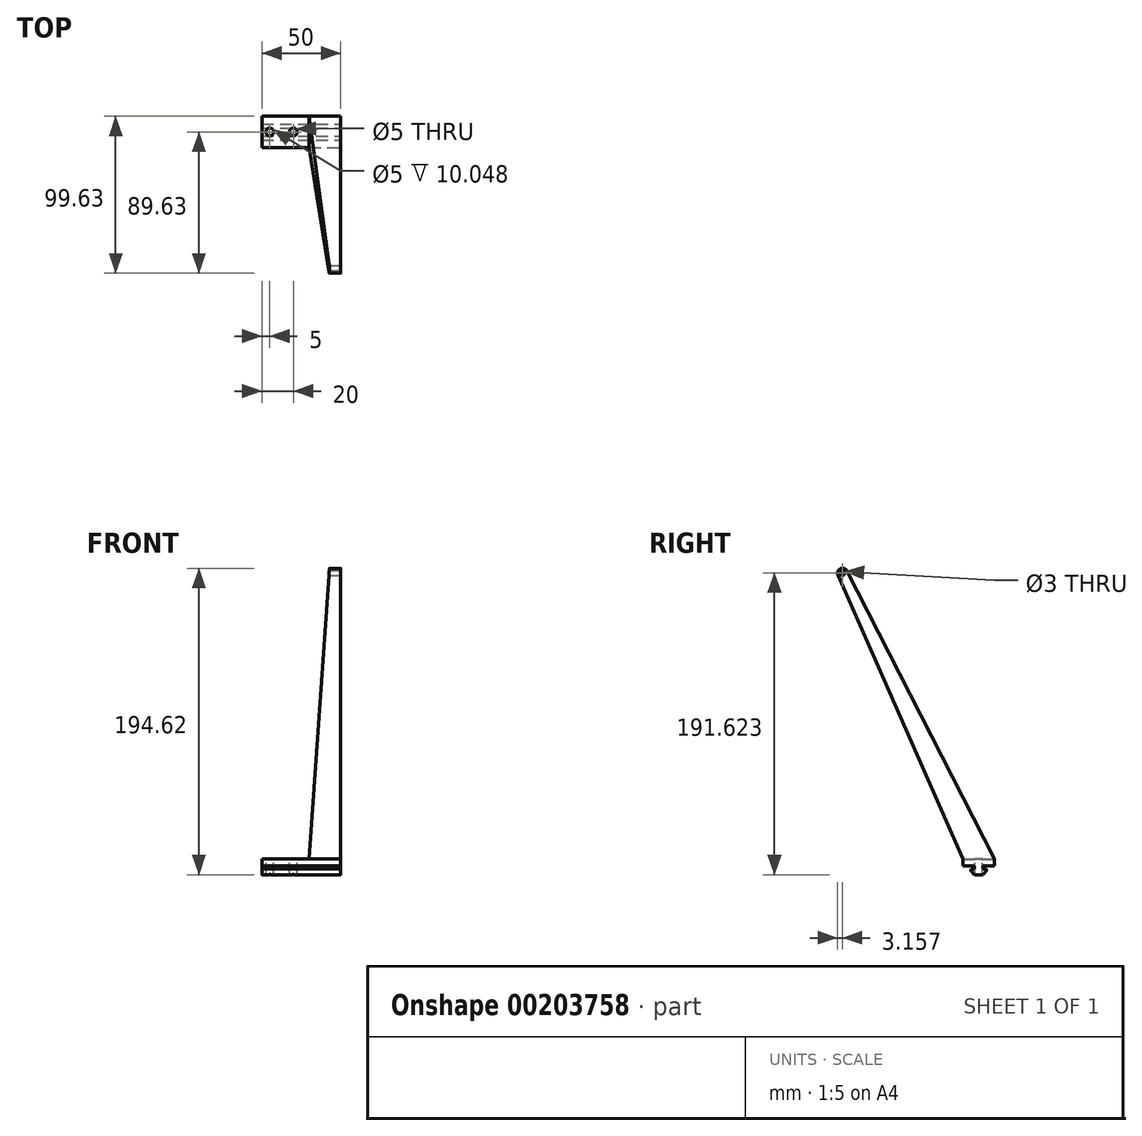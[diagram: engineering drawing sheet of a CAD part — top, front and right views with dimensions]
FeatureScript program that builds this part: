
annotation { "Feature Type Name" : "Feature", "Feature Type Description" : "" }
export const myFeature = defineFeature(function(context is Context, id is Id, definition is map)
    precondition{}
    {
        {
            var Q0;
            Q0=qCreatedBy(makeId("Right.planeOp"),FACE);
            var sketch = newSketch(context, id + "F0", { "sketchPlane" : qUnion([Q0])});
            skLineSegment(sketch, "E0.top", {"start": v(10, 2.22) * mm, "end": v(-10, 2.22) * mm});
            skLineSegment(sketch, "E0.left", {"start": v(10, -2.22) * mm, "end": v(10, 2.22) * mm});
            skLineSegment(sketch, "E0.right", {"start": v(-10, -2.22) * mm, "end": v(-10, 2.22) * mm});
            skPoint(sketch, "E0.middle", {"position": v(0, 0) * mm});
            skLineSegment(sketch, "E1", {"start": v(-10, 2.22) * mm, "end": v(-89.38, 182.52) * mm});
            skLineSegment(sketch, "E2", {"start": v(-87.84, 186.48) * mm, "end": v(-87.68, 186.55) * mm});
            skLineSegment(sketch, "E3", {"start": v(-83.8, 185.17) * mm, "end": v(10, 2.22) * mm});
            skLineSegment(sketch, "E4", {"start": v(0, -2.22) * mm, "end": v(0, -12.22) * mm, "construction": true});
            skLineSegment(sketch, "E5", {"start": v(0, -12.22) * mm, "end": v(-10, -2.22) * mm, "construction": true});
            skPoint(sketch, "E6.visualSharp", {"position": v(-90.58, 185.27) * mm});
            skArc(sketch, "E6.filletArc", {"start": v(-87.84, 186.48) * mm, "mid": v(-89.43, 184.82) * mm, "end": v(-89.38, 182.52) * mm});
            skPoint(sketch, "E7.visualSharp", {"position": v(-85.1, 187.69) * mm});
            skArc(sketch, "E7.filletArc", {"start": v(-83.8, 185.17) * mm, "mid": v(-85.47, 186.63) * mm, "end": v(-87.68, 186.55) * mm});
            skLineSegment(sketch, "E8", {"start": v(-10, -2.22) * mm, "end": v(-2.6, -2.22) * mm});
            skLineSegment(sketch, "E9", {"start": v(-2.6, -2.22) * mm, "end": v(-2.6, -4.22) * mm});
            skLineSegment(sketch, "E10", {"start": v(-2.6, -4.22) * mm, "end": v(-5, -4.22) * mm});
            skLineSegment(sketch, "E11", {"start": v(-5, -4.22) * mm, "end": v(-5, -5.04) * mm});
            skLineSegment(sketch, "E12.trimOffspring", {"start": v(-2.63, -7.82) * mm, "end": v(-0.36, -7.82) * mm, "construction": true});
            skLineSegment(sketch, "E13.trimOffspring", {"start": v(-2.93, -7.53) * mm, "end": v(-4.7, -5.75) * mm});
            skLineSegment(sketch, "E14.MirrorCS", {"start": v(10, -2.22) * mm, "end": v(2.6, -2.22) * mm});
            skLineSegment(sketch, "E15.MirrorCS", {"start": v(2.6, -2.22) * mm, "end": v(2.6, -4.22) * mm});
            skLineSegment(sketch, "E16.MirrorCS", {"start": v(2.6, -4.22) * mm, "end": v(5, -4.22) * mm});
            skLineSegment(sketch, "E17.MirrorCS", {"start": v(5, -4.22) * mm, "end": v(5, -5.04) * mm});
            skLineSegment(sketch, "E18.MirrorCS", {"start": v(2.93, -7.53) * mm, "end": v(4.7, -5.75) * mm});
            skLineSegment(sketch, "E19", {"start": v(-2.22, -7.82) * mm, "end": v(2.22, -7.82) * mm});
            skPoint(sketch, "E20.visualSharp", {"position": v(2.63, -7.82) * mm});
            skArc(sketch, "E20.filletArc", {"start": v(2.22, -7.82) * mm, "mid": v(2.6, -7.75) * mm, "end": v(2.93, -7.53) * mm});
            skPoint(sketch, "E21.visualSharp", {"position": v(5, -5.46) * mm});
            skArc(sketch, "E21.filletArc", {"start": v(4.7, -5.75) * mm, "mid": v(4.92, -5.42) * mm, "end": v(5, -5.04) * mm});
            skPoint(sketch, "E22.visualSharp", {"position": v(-2.63, -7.82) * mm});
            skArc(sketch, "E22.filletArc", {"start": v(-2.93, -7.53) * mm, "mid": v(-2.6, -7.75) * mm, "end": v(-2.22, -7.82) * mm});
            skPoint(sketch, "E23.visualSharp", {"position": v(-5, -5.46) * mm});
            skArc(sketch, "E23.filletArc", {"start": v(-5, -5.04) * mm, "mid": v(-4.92, -5.42) * mm, "end": v(-4.7, -5.75) * mm});
            skSolve(sketch);
        }
        {
            var Q0;
            Q0=makeQuery(id+"F0.imprint","IMPRINT",FACE,{"disambiguationData":[TD([[makeQuery(id+"F0.imprint","IMPRINT",EDGE,{"derivedFrom":sQuery(id+"F0.wireOp",EDGE,"E0.top")}),1.0]])]});
            extrude(context, id + "F1", {"entities" : qUnion([Q0]), "oppositeDirection" : true, "depth" : 50 * mm});
        }
        {
            var Q0;
            Q0 = qSketchRegion(id + "F0", true);
            extrude(context, id + "F2", {"entities" : qUnion([Q0]), "operationType" : NewBodyOperationType.ADD, "oppositeDirection" : true, "depth" : 20 * mm});
        }
        {
            var Q0;
            Q0=qCreatedBy(makeId("Front.planeOp"),FACE);
            cPlane(context, id + "F3", {"entities" : qUnion([Q0]), "cplaneType" : CPlaneType.OFFSET, "offset" : 10 * mm, "oppositeDirection" : true, "width" : 150 * mm, "height" : 150 * mm});
        }
        {
            var Q0;
            Q0=qCreatedBy(id+"F3.planeOp",FACE);
            var sketch = newSketch(context, id + "F4", { "sketchPlane" : qUnion([Q0])});
            skLineSegment(sketch, "E24", {"start": v(0, 0) * mm, "end": v(0, 2) * mm, "construction": true});
            skLineSegment(sketch, "E25", {"start": v(0, 2) * mm, "end": v(-6, 2) * mm, "construction": true});
            skLineSegment(sketch, "E26", {"start": v(-6, 2) * mm, "end": v(-6, 202.68) * mm, "construction": true});
            skLineSegment(sketch, "E27", {"start": v(-6, 2) * mm, "end": v(-20, 2) * mm});
            skLineSegment(sketch, "E28", {"start": v(-20, 2) * mm, "end": v(-6, 202.68) * mm});
            skLineSegment(sketch, "E29", {"start": v(-6, 202.68) * mm, "end": v(-20, 203.66) * mm});
            skLineSegment(sketch, "E30", {"start": v(-20, 2) * mm, "end": v(-20, 203.66) * mm});
            skSolve(sketch);
        }
        {
            var Q0;
            Q0=makeQuery(id+"F4.imprint","IMPRINT",FACE,{"disambiguationData":[TD([[makeQuery(id+"F4.imprint","IMPRINT",EDGE,{"derivedFrom":sQuery(id+"F4.wireOp",EDGE,"E28")}),1.0]])]});
            extrude(context, id + "F5", {"entities" : qUnion([Q0]), "operationType" : NewBodyOperationType.REMOVE, "endBound" : BoundingType.THROUGH_ALL, "depth" : 25 * mm});
        }
        {
            var Q0;
            {var subQ0=sQuery(id+"F0.wireOp",EDGE,"E23.filletArc");var subQ1=sQuery(id+"F0.wireOp",EDGE,"E22.filletArc");var subQ2=sQuery(id+"F0.wireOp",EDGE,"E21.filletArc");var subQ3=sQuery(id+"F0.wireOp",EDGE,"E20.filletArc");var subQ4=sQuery(id+"F0.wireOp",EDGE,"E19");var subQ5=sQuery(id+"F0.wireOp",EDGE,"E18.MirrorCS");var subQ6=sQuery(id+"F0.wireOp",EDGE,"E17.MirrorCS");var subQ7=sQuery(id+"F0.wireOp",EDGE,"E16.MirrorCS");var subQ8=sQuery(id+"F0.wireOp",EDGE,"E15.MirrorCS");var subQ9=sQuery(id+"F0.wireOp",EDGE,"E14.MirrorCS");var subQ10=sQuery(id+"F0.wireOp",EDGE,"E13.trimOffspring");var subQ11=sQuery(id+"F0.wireOp",EDGE,"E11");var subQ12=sQuery(id+"F0.wireOp",EDGE,"E10");var subQ13=sQuery(id+"F0.wireOp",EDGE,"E9");var subQ14=sQuery(id+"F0.wireOp",EDGE,"E8");var subQ15=sQuery(id+"F0.wireOp",EDGE,"E0.right");var subQ16=sQuery(id+"F0.wireOp",EDGE,"E0.left");Q0=makeQuery(id+"F2.boolean.opBoolean","MERGE",FACE,{"derivedFrom":[makeQuery(id+"F1.opExtrude","CAP_FACE",FACE,{"disambiguationData":[OSD([sQuery(id+"F0.wireOp",EDGE,"E0.top"),subQ16,subQ15,subQ14,subQ13,subQ12,subQ11,subQ10,subQ9,subQ8,subQ7,subQ6,subQ5,subQ4,subQ3,subQ2,subQ1,subQ0])],"isStart":true}),makeQuery(id+"F2.opExtrude","CAP_FACE",FACE,{"disambiguationData":[OSD([subQ16,subQ15,sQuery(id+"F0.wireOp",EDGE,"E1"),sQuery(id+"F0.wireOp",EDGE,"E2"),sQuery(id+"F0.wireOp",EDGE,"E3"),sQuery(id+"F0.wireOp",EDGE,"E6.filletArc"),sQuery(id+"F0.wireOp",EDGE,"E7.filletArc"),subQ14,subQ13,subQ12,subQ11,subQ10,subQ9,subQ8,subQ7,subQ6,subQ5,subQ4,subQ3,subQ2,subQ1,subQ0])],"isStart":true})]});}
            var sketch = newSketch(context, id + "F6", { "sketchPlane" : qUnion([Q0])});
            skCircle(sketch, "E31", {"center": v(-86.47, 183.8) * mm, "radius": 1.5 * mm});
            skSolve(sketch);
        }
        {
            var Q0;
            Q0=makeQuery(id+"F6.imprint","IMPRINT",FACE,{"disambiguationData":[TD([[makeQuery(id+"F6.imprint","IMPRINT",EDGE,{"derivedFrom":sQuery(id+"F6.wireOp",EDGE,"E31")}),1.0]])]});
            extrude(context, id + "F7", {"entities" : qUnion([Q0]), "operationType" : NewBodyOperationType.REMOVE, "endBound" : BoundingType.UP_TO_NEXT, "oppositeDirection" : true, "depth" : 25 * mm});
        }
        {
            var Q0;
            Q0=makeQuery(id+"F1.opExtrude","SWEPT_FACE",FACE,{"disambiguationData":[OSD([sQuery(id+"F0.wireOp",EDGE,"E0.top")])]});
            var sketch = newSketch(context, id + "F8", { "sketchPlane" : qUnion([Q0])});
            skLineSegment(sketch, "E32", {"start": v(-50, 10) * mm, "end": v(-45, 10) * mm, "construction": true});
            skLineSegment(sketch, "E33", {"start": v(-45, 10) * mm, "end": v(-45, -16.73) * mm, "construction": true});
            skLineSegment(sketch, "E34", {"start": v(-45, -16.73) * mm, "end": v(-30, -16.73) * mm, "construction": true});
            skLineSegment(sketch, "E35", {"start": v(-30, -16.73) * mm, "end": v(-30, 20.13) * mm, "construction": true});
            skLineSegment(sketch, "E36", {"start": v(-50, 0) * mm, "end": v(-23.96, 0) * mm, "construction": true});
            skPoint(sketch, "E36.endSnap0", {"position": v(-50, 0) * mm});
            skCircle(sketch, "E37", {"center": v(-45, 0) * mm, "radius": 2.5 * mm});
            skCircle(sketch, "E38", {"center": v(-30, 0) * mm, "radius": 2.5 * mm});
            skSolve(sketch);
        }
        {
            var Q0;
            Q0=makeQuery(id+"F8.imprint","IMPRINT",FACE,{"disambiguationData":[TD([[makeQuery(id+"F8.imprint","IMPRINT",EDGE,{"derivedFrom":sQuery(id+"F8.wireOp",EDGE,"E37")}),1.0]])]});
            var Q1;
            Q1=makeQuery(id+"F8.imprint","IMPRINT",FACE,{"disambiguationData":[TD([[makeQuery(id+"F8.imprint","IMPRINT",EDGE,{"derivedFrom":sQuery(id+"F8.wireOp",EDGE,"E38")}),1.0]])]});
            var Q2;
            Q2=sQuery(id+"F8.wireOp",EDGE,"E37");
            var Q3;
            Q3=sQuery(id+"F8.wireOp",EDGE,"E38");
            extrude(context, id + "F9", {"entities" : qUnion([Q0, Q1]), "operationType" : NewBodyOperationType.REMOVE, "surfaceEntities" : qUnion([Q2, Q3]), "endBound" : BoundingType.UP_TO_NEXT, "oppositeDirection" : true, "depth" : 25 * mm});
        }
    });
